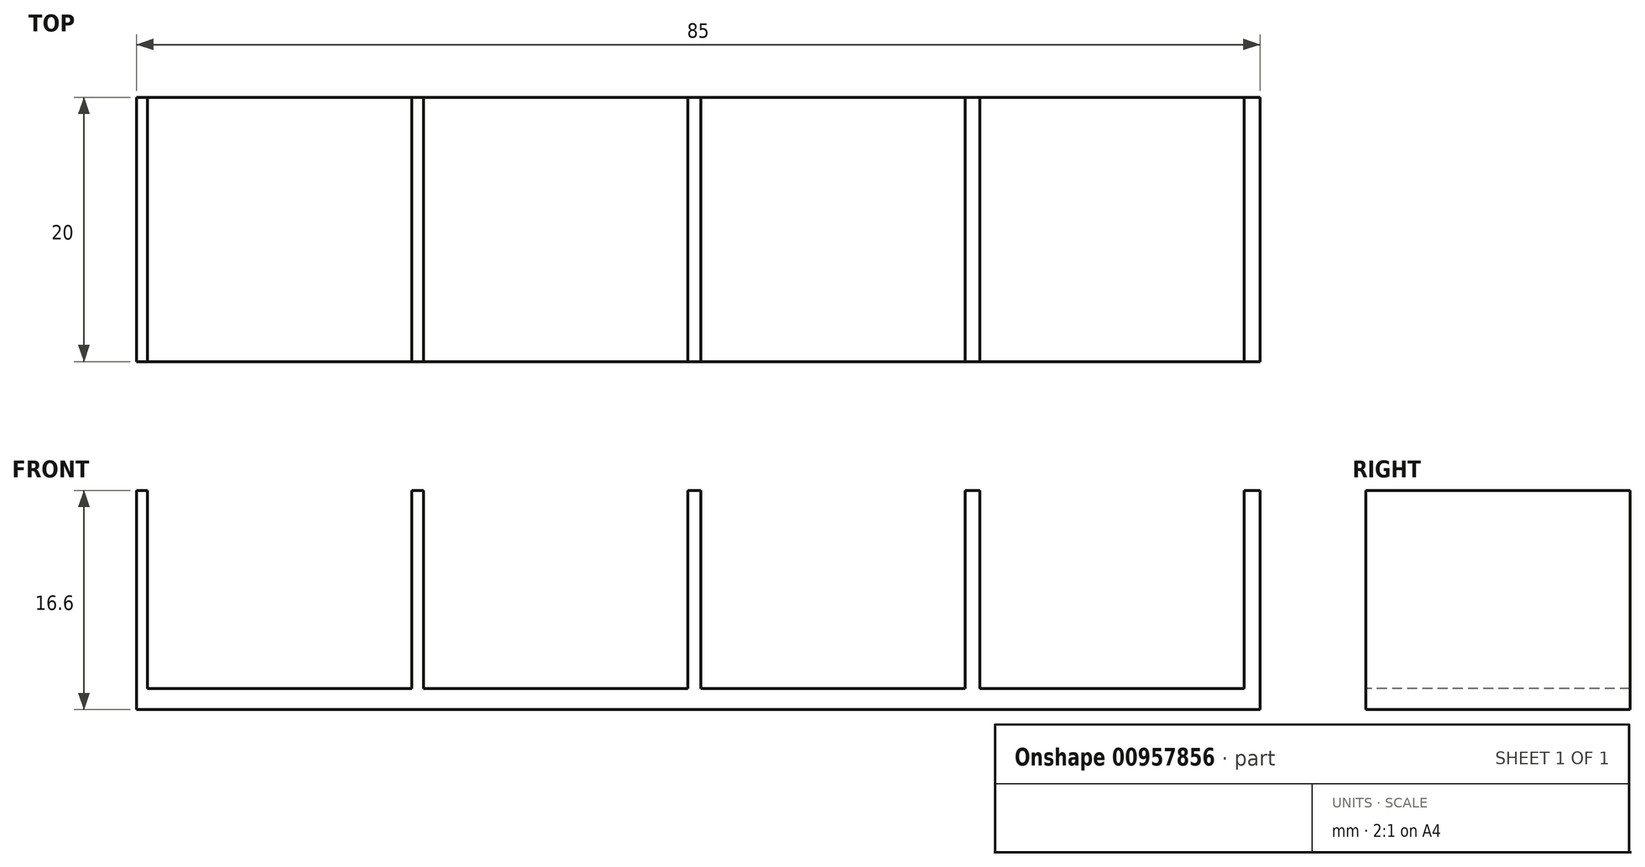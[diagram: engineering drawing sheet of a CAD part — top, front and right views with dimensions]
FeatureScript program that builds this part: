
annotation { "Feature Type Name" : "Feature", "Feature Type Description" : "" }
export const myFeature = defineFeature(function(context is Context, id is Id, definition is map)
    precondition{}
    {
        {
            var Q0;
            Q0=qCreatedBy(makeId("Top.planeOp"),FACE);
            var sketch = newSketch(context, id + "F0", { "sketchPlane" : qUnion([Q0])});
            skLineSegment(sketch, "E0.bottom", {"start": v(0, 0) * mm, "end": v(85, 0) * mm});
            skLineSegment(sketch, "E0.top", {"start": v(0, -20) * mm, "end": v(85, -20) * mm});
            skLineSegment(sketch, "E0.left", {"start": v(0, 0) * mm, "end": v(0, -20) * mm});
            skLineSegment(sketch, "E0.right", {"start": v(85, 0) * mm, "end": v(85, -20) * mm});
            skSolve(sketch);
        }
        {
            var Q0;
            Q0=makeQuery(id+"F0.imprint","IMPRINT",FACE,{"disambiguationData":[TD([[makeQuery(id+"F0.imprint","IMPRINT",EDGE,{"derivedFrom":sQuery(id+"F0.wireOp",EDGE,"E0.bottom")}),-1.0]])]});
            extrude(context, id + "F1", {"entities" : qUnion([Q0]), "depth" : 1.6 * mm, "offsetDistance" : 25 * mm});
        }
        {
            var Q0;
            Q0=makeQuery(id+"F1.opExtrude","CAP_FACE",FACE,{"disambiguationData":[OSD([sQuery(id+"F0.wireOp",EDGE,"E0.bottom"),sQuery(id+"F0.wireOp",EDGE,"E0.top"),sQuery(id+"F0.wireOp",EDGE,"E0.left"),sQuery(id+"F0.wireOp",EDGE,"E0.right")])],"isStart":false});
            var sketch = newSketch(context, id + "F2", { "sketchPlane" : qUnion([Q0])});
            skLineSegment(sketch, "E1", {"start": v(0, 0) * mm, "end": v(0, -20) * mm});
            skLineSegment(sketch, "E2.0", {"start": v(0.8, 5) * mm, "end": v(0.8, -20) * mm});
            skLineSegment(sketch, "E3.0", {"start": v(20.8, 5) * mm, "end": v(20.8, -20) * mm});
            skLineSegment(sketch, "E4.0", {"start": v(21.7, 5) * mm, "end": v(21.7, -20) * mm});
            skLineSegment(sketch, "E5.0", {"start": v(41.7, 5) * mm, "end": v(41.7, -20) * mm});
            skLineSegment(sketch, "E6.0", {"start": v(42.7, 5) * mm, "end": v(42.7, -20) * mm});
            skLineSegment(sketch, "E7.0", {"start": v(62.7, 5) * mm, "end": v(62.7, -20) * mm});
            skLineSegment(sketch, "E8.0", {"start": v(63.8, 5) * mm, "end": v(63.8, -20) * mm});
            skLineSegment(sketch, "E9.0", {"start": v(83.8, 5) * mm, "end": v(83.8, -20) * mm});
            skLineSegment(sketch, "E10.0", {"start": v(85, 5) * mm, "end": v(85, -20) * mm});
            skSolve(sketch);
        }
        {
            var Q0;
            {var subQ0=sQuery(id+"F2.wireOp",EDGE,"E1");Q0=makeQuery(id+"F2.imprint","IMPRINT",FACE,{"disambiguationData":[TD([[makeQuery(id+"F2.imprint","IMPRINT",EDGE,{"derivedFrom":subQ0}),1.0]])]});}
            var Q1;
            {var subQ0=sQuery(id+"F2.wireOp",EDGE,"E3.0");Q1=makeQuery(id+"F2.imprint","IMPRINT",FACE,{"disambiguationData":[TD([[makeQuery(id+"F2.imprint","IMPRINT",EDGE,{"derivedFrom":subQ0}),1.0]])]});}
            var Q2;
            {var subQ0=sQuery(id+"F2.wireOp",EDGE,"E5.0");Q2=makeQuery(id+"F2.imprint","IMPRINT",FACE,{"disambiguationData":[TD([[makeQuery(id+"F2.imprint","IMPRINT",EDGE,{"derivedFrom":subQ0}),1.0]])]});}
            var Q3;
            {var subQ0=sQuery(id+"F2.wireOp",EDGE,"E7.0");Q3=makeQuery(id+"F2.imprint","IMPRINT",FACE,{"disambiguationData":[TD([[makeQuery(id+"F2.imprint","IMPRINT",EDGE,{"derivedFrom":subQ0}),1.0]])]});}
            var Q4;
            {var subQ0=sQuery(id+"F2.wireOp",EDGE,"E9.0");Q4=makeQuery(id+"F2.imprint","IMPRINT",FACE,{"disambiguationData":[TD([[makeQuery(id+"F2.imprint","IMPRINT",EDGE,{"derivedFrom":subQ0}),1.0]])]});}
            extrude(context, id + "F3", {"entities" : qUnion([Q0, Q1, Q2, Q3, Q4]), "operationType" : NewBodyOperationType.ADD, "depth" : 15 * mm, "offsetDistance" : 25 * mm});
        }
    });
